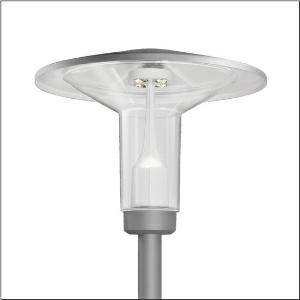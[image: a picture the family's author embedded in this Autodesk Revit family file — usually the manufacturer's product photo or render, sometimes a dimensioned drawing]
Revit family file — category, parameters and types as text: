
# Revit family: laterne_iq___p1_0a_5xa5255nf14h_4412
name_source: partatom
category: Lighting Fixtures
units: mm (PartAtom-declared; Revit-internal decimal feet)

## family parameters
Cut with Voids When Loaded = No
Host = Face
Light Source = No
Part Type = Normal
Room Calculation Point = No
Round Connector Dimension = Use Diameter
Shared = No

## types (1)
- --- (1 x LED, 1510 lm, 11.8 W, 2700K)
    Apparent Load = 12 VA
    CIE Flux Codes = 35 64 91 96 100
    Color Rendering = 70
    Color Temperature = 2700K
    Default Elevation = 1800 mm
    Description = Lantern iQ, mast luminaire, Module 540 iQ-SR, primary light control with 3 zone facetted reflector, of plastic, silver coated, highly specular, structured, primary optical cover: cover, of PMMA, transparent, light distribution: P1.0a, light emission: direct distribution, primary light characteristic: strongly asymmetric, installation type: post-top, LED, High Power LED, rated luminous flux: 1.510lm, luminous efficacy: 128lm/W, light colour: 727, colour temperature: 2700K, control gear: ECG iQ, control: presetting dimming logarithmic, Street-Remote, Auto-Match, Temp-Guard, Lumen-Switch, Night-Set, Smart-Wire, Light-Fading, Desk-Remote (wireless, voltage-free reading and setting of iQ features in the workshop via application-optimized NFC function/RFID function), optimised constant luminous flux control (CLO 2.0), with terminal, 6-pole, max. 2.5mm², mains connection: 230..240V, AC, 50/60Hz, start of lifetime: 12W, end of service life: 12W, reduction: 6W, luminaire housing, upper part, of glass-fibre reinforced polyester, coated, Siteco® metallic grey (DB 702S), diameter: 750mm, height: 583mm, spigot size: d x l = 76 x 70mm (post-top) | with reducer (optional accessory) 60 x 70mm, post-top mast mounting element, of diecast aluminium, coated, Siteco® metallic grey (DB 702S), Module 540 iQ-SR, traffic white (RAL 9016), equipment: standard, protection rating (complete): IP65, insulation class (complete): insulation class II (safety insulation), certification: CE, ENEC, VDE, packaging unit: 1 piece

Light Distribution: P1.0a
    Height = 583 mm
    Lamp = 1 x LED
    Lamp Light Flux = 1510 lm
    Lamp Power = 11.8 W
    Lamp count = 1
    Length = 750 mm
    Luminous efficacy = 128 lm/W
    Manufacturer = Siteco
    ModVariant = No
    Model = 5XA5255NF14H
    Number of Poles = 1
    OnlyDefault = Yes
    Power Factor = 1
    Product Name = Laterne iQ | P1.0a
    Product group = mast luminaire | pylon top
    ProductGroupID = 6100
    Protection Class = Protection class II
    Protection Degree = IP 65
    RLX_Detail_Level = 1
    RLX_Emergency_Light_Flux = 0 lm
    RLX_Emergency_Type = 0
    RLX_Emergency_Type_DB = No
    RlxData = <blob elided: 73877 chars, md5=abaf1122>
    Socket = socket
    Standby Power = 0 W
    System Light Flux = 1510 lm
    System Power = 12 W
    Type Comments = factory setting: luminous flux: 100 % | dim-lin: 254 | 472 mA
    Type Image = l_1006050.jpg
    URL = http://relux.com
    VarID = @adj_103531
    Voltage = 0 V
    Weight = 0.00 kg
    Width = 0 mm  [stored 0 ft]

note: [stored X ft] marks values corroborated as IEEE doubles in the binary element streams (Revit-internal decimal feet)

## geometry (parser evidence)
native form markers: Blend x4, Sweep x8
no freeform markers — native parametric forms only
